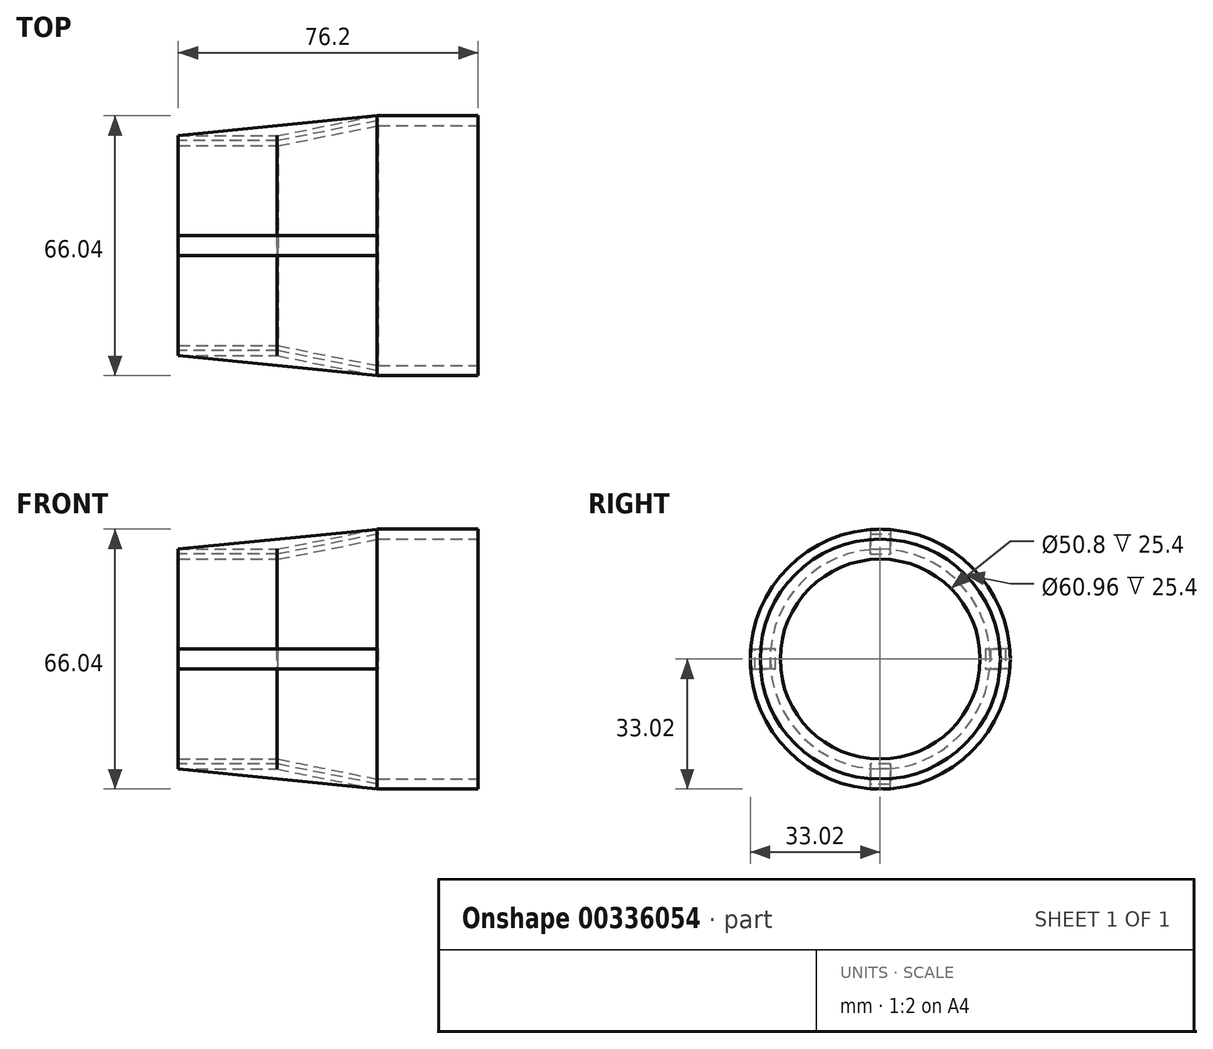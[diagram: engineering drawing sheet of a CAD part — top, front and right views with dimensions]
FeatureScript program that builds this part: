
annotation { "Feature Type Name" : "Feature", "Feature Type Description" : "" }
export const myFeature = defineFeature(function(context is Context, id is Id, definition is map)
    precondition{}
    {
        {
            var Q0;
            Q0=qCreatedBy(makeId("Front.planeOp"),FACE);
            var sketch = newSketch(context, id + "F0", { "sketchPlane" : qUnion([Q0])});
            skLineSegment(sketch, "E0", {"start": v(9.46, 25.4) * mm, "end": v(-15.94, 25.4) * mm});
            skLineSegment(sketch, "E1", {"start": v(-15.94, 27.94) * mm, "end": v(-15.94, 25.4) * mm});
            skLineSegment(sketch, "E2", {"start": v(34.86, 30.48) * mm, "end": v(9.46, 25.4) * mm});
            skLineSegment(sketch, "E3", {"start": v(60.26, 30.48) * mm, "end": v(34.86, 30.48) * mm});
            skLineSegment(sketch, "E4", {"start": v(77.13, 0) * mm, "end": v(-57.88, 0) * mm, "construction": true});
            skLineSegment(sketch, "E5.0", {"start": v(34.6, 33.02) * mm, "end": v(9.2, 27.94) * mm});
            skLineSegment(sketch, "E6.0", {"start": v(60.26, 33.02) * mm, "end": v(34.6, 33.02) * mm});
            skLineSegment(sketch, "E7.0", {"start": v(9.2, 27.94) * mm, "end": v(-15.94, 27.94) * mm});
            skLineSegment(sketch, "E8", {"start": v(60.26, 33.02) * mm, "end": v(60.26, 30.48) * mm});
            skPoint(sketch, "E9.end.orphan", {"position": v(47.56, 30.48) * mm});
            skLineSegment(sketch, "E10", {"start": v(-15.94, 27.94) * mm, "end": v(34.6, 33.02) * mm});
            skSolve(sketch);
        }
        {
            var Q0;
            Q0=makeQuery(id+"F0.imprint","IMPRINT",FACE,{"disambiguationData":[TD([[makeQuery(id+"F0.imprint","IMPRINT",EDGE,{"derivedFrom":sQuery(id+"F0.wireOp",EDGE,"E0")}),-1.0]])]});
            var Q1;
            Q1=sQuery(id+"F0.wireOp",EDGE,"E4");
            revolve(context, id + "F1", {"entities" : qUnion([Q0]), "axis" : qUnion([Q1]), "revolveType" : RevolveType.FULL});
        }
        {
            var Q0;
            Q0=qCreatedBy(makeId("Front.planeOp"),FACE);
            var sketch = newSketch(context, id + "F2", { "sketchPlane" : qUnion([Q0])});
            skLineSegment(sketch, "E11.0", {"start": v(9.33, 26.67) * mm, "end": v(-15.94, 26.67) * mm});
            skLineSegment(sketch, "E12.0", {"start": v(34.82, 31.77) * mm, "end": v(9.33, 26.67) * mm});
            skLineSegment(sketch, "E13", {"start": v(-15.94, 26.67) * mm, "end": v(-15.94, 27.94) * mm});
            skLineSegment(sketch, "E14", {"start": v(34.57, 33.01) * mm, "end": v(34.82, 31.77) * mm});
            skLineSegment(sketch, "E15", {"start": v(-15.94, 27.94) * mm, "end": v(34.57, 33.01) * mm});
            skSolve(sketch);
        }
        {
            var Q0;
            Q0=makeQuery(id+"F2.imprint","IMPRINT",FACE,{"disambiguationData":[TD([[makeQuery(id+"F2.imprint","IMPRINT",EDGE,{"derivedFrom":sQuery(id+"F2.wireOp",EDGE,"E11.0")}),-1.0]])]});
            extrude(context, id + "F3", {"entities" : qUnion([Q0]), "endBound" : BoundingType.SYMMETRIC, "depth" : 5.08 * mm});
        }
        {
            var Q0;
            Q0=makeQuery(id+"F3.opExtrude","SWEPT_BODY",BODY,{"disambiguationData":[OSD([sQuery(id+"F2.wireOp",EDGE,"E11.0"),sQuery(id+"F2.wireOp",EDGE,"E12.0"),sQuery(id+"F2.wireOp",EDGE,"E13"),sQuery(id+"F2.wireOp",EDGE,"E14"),sQuery(id+"F2.wireOp",EDGE,"E15")])]});
            var Q1;
            Q1=sQuery(id+"F0.wireOp",EDGE,"E4");
            circularPattern(context, id + "F4", {"entities" : qUnion([Q0]), "axis" : qUnion([Q1]), "angle" : 360 * degree, "instanceCount" : 4, "equalSpace" : true});
        }
    });
